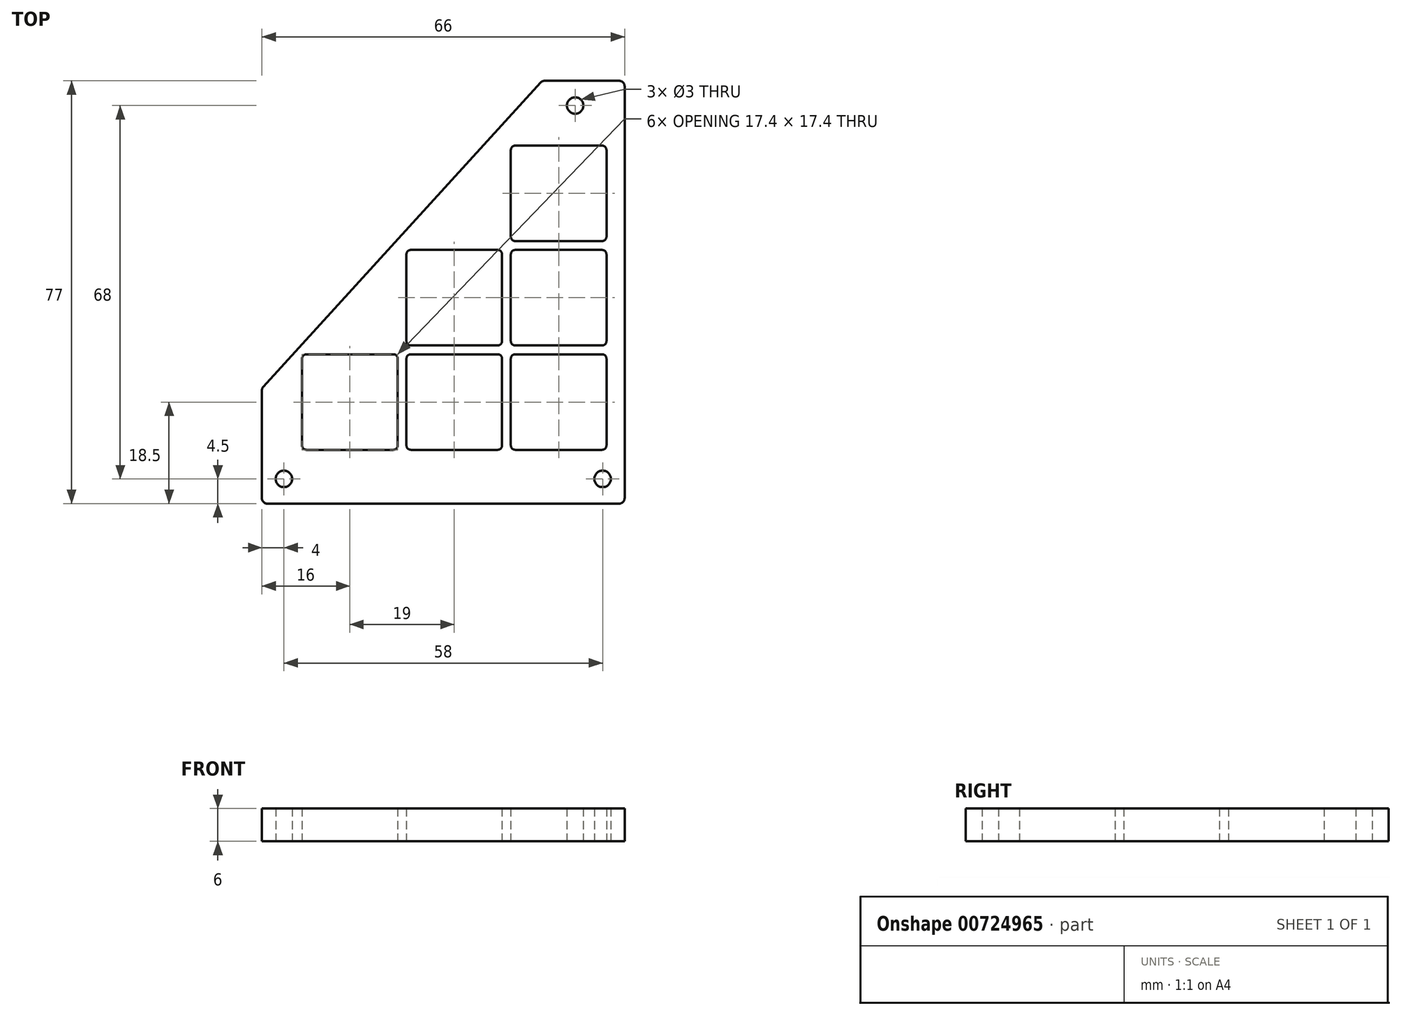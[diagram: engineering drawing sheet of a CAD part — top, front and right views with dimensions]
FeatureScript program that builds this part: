
annotation { "Feature Type Name" : "Feature", "Feature Type Description" : "" }
export const myFeature = defineFeature(function(context is Context, id is Id, definition is map)
    precondition{}
    {
        {
            var Q0;
            Q0=qCreatedBy(makeId("Top.planeOp"),FACE);
            var sketch = newSketch(context, id + "F0", { "sketchPlane" : qUnion([Q0])});
            skLineSegment(sketch, "E0", {"start": v(0, 0) * mm, "end": v(66, 0) * mm});
            skLineSegment(sketch, "E1", {"start": v(66, 0) * mm, "end": v(66, 77) * mm});
            skLineSegment(sketch, "E2", {"start": v(66, 77) * mm, "end": v(51, 77) * mm});
            skLineSegment(sketch, "E3", {"start": v(0, 0) * mm, "end": v(0, 21) * mm});
            skLineSegment(sketch, "E4", {"start": v(0, 21) * mm, "end": v(51, 77) * mm});
            skCircle(sketch, "E5", {"center": v(4, 4.5) * mm, "radius": 1.5 * mm});
            skCircle(sketch, "E6", {"center": v(57, 72.5) * mm, "radius": 1.5 * mm});
            skCircle(sketch, "E7", {"center": v(62, 4.5) * mm, "radius": 1.5 * mm});
            skLineSegment(sketch, "E8.bottom", {"start": v(24.7, 9.8) * mm, "end": v(7.3, 9.8) * mm});
            skLineSegment(sketch, "E8.top", {"start": v(24.7, 27.2) * mm, "end": v(7.3, 27.2) * mm});
            skLineSegment(sketch, "E8.left", {"start": v(24.7, 9.8) * mm, "end": v(24.7, 27.2) * mm});
            skLineSegment(sketch, "E8.right", {"start": v(7.3, 9.8) * mm, "end": v(7.3, 27.2) * mm});
            skPoint(sketch, "E8.middle", {"position": v(16, 18.5) * mm});
            skLineSegment(sketch, "E9.bottom", {"start": v(43.7, 9.8) * mm, "end": v(26.3, 9.8) * mm});
            skLineSegment(sketch, "E9.top", {"start": v(43.7, 27.2) * mm, "end": v(26.3, 27.2) * mm});
            skLineSegment(sketch, "E9.left", {"start": v(43.7, 9.8) * mm, "end": v(43.7, 27.2) * mm});
            skLineSegment(sketch, "E9.right", {"start": v(26.3, 9.8) * mm, "end": v(26.3, 27.2) * mm});
            skPoint(sketch, "E9.middle", {"position": v(35, 18.5) * mm});
            skLineSegment(sketch, "E10.bottom", {"start": v(62.7, 9.8) * mm, "end": v(45.3, 9.8) * mm});
            skLineSegment(sketch, "E10.top", {"start": v(62.7, 27.2) * mm, "end": v(45.3, 27.2) * mm});
            skLineSegment(sketch, "E10.left", {"start": v(62.7, 9.8) * mm, "end": v(62.7, 27.2) * mm});
            skLineSegment(sketch, "E10.right", {"start": v(45.3, 9.8) * mm, "end": v(45.3, 27.2) * mm});
            skPoint(sketch, "E10.middle", {"position": v(54, 18.5) * mm});
            skLineSegment(sketch, "E11.bottom", {"start": v(43.7, 28.8) * mm, "end": v(26.3, 28.8) * mm});
            skLineSegment(sketch, "E11.top", {"start": v(43.7, 46.2) * mm, "end": v(26.3, 46.2) * mm});
            skLineSegment(sketch, "E11.left", {"start": v(43.7, 28.8) * mm, "end": v(43.7, 46.2) * mm});
            skLineSegment(sketch, "E11.right", {"start": v(26.3, 28.8) * mm, "end": v(26.3, 46.2) * mm});
            skPoint(sketch, "E11.middle", {"position": v(35, 37.5) * mm});
            skLineSegment(sketch, "E12.bottom", {"start": v(62.7, 28.8) * mm, "end": v(45.3, 28.8) * mm});
            skLineSegment(sketch, "E12.top", {"start": v(62.7, 46.2) * mm, "end": v(45.3, 46.2) * mm});
            skLineSegment(sketch, "E12.left", {"start": v(62.7, 28.8) * mm, "end": v(62.7, 46.2) * mm});
            skLineSegment(sketch, "E12.right", {"start": v(45.3, 28.8) * mm, "end": v(45.3, 46.2) * mm});
            skPoint(sketch, "E12.middle", {"position": v(54, 37.5) * mm});
            skLineSegment(sketch, "E13.bottom", {"start": v(62.7, 47.8) * mm, "end": v(45.3, 47.8) * mm});
            skLineSegment(sketch, "E13.top", {"start": v(62.7, 65.2) * mm, "end": v(45.3, 65.2) * mm});
            skLineSegment(sketch, "E13.left", {"start": v(62.7, 47.8) * mm, "end": v(62.7, 65.2) * mm});
            skLineSegment(sketch, "E13.right", {"start": v(45.3, 47.8) * mm, "end": v(45.3, 65.2) * mm});
            skPoint(sketch, "E13.middle", {"position": v(54, 56.5) * mm});
            skSolve(sketch);
        }
        {
            var Q0;
            Q0=makeQuery(id+"F0.imprint","IMPRINT",FACE,{"disambiguationData":[TD([[makeQuery(id+"F0.imprint","IMPRINT",EDGE,{"derivedFrom":sQuery(id+"F0.wireOp",EDGE,"E0")}),1.0]])]});
            extrude(context, id + "F1", {"entities" : qUnion([Q0]), "depth" : 6 * mm, "offsetDistance" : 25 * mm});
        }
        {
            var Q0;
            Q0=makeQuery(id+"F1.opExtrude","SWEPT_EDGE",EDGE,{"disambiguationData":[OSD([sQuery(id+"F0.wireOp",EDGE,"E8.top"),sQuery(id+"F0.wireOp",EDGE,"E8.right")])]});
            var Q1;
            Q1=makeQuery(id+"F1.opExtrude","SWEPT_EDGE",EDGE,{"disambiguationData":[OSD([sQuery(id+"F0.wireOp",EDGE,"E9.top"),sQuery(id+"F0.wireOp",EDGE,"E9.right")])]});
            var Q2;
            Q2=makeQuery(id+"F1.opExtrude","SWEPT_EDGE",EDGE,{"disambiguationData":[OSD([sQuery(id+"F0.wireOp",EDGE,"E10.top"),sQuery(id+"F0.wireOp",EDGE,"E10.right")])]});
            var Q3;
            Q3=makeQuery(id+"F1.opExtrude","SWEPT_EDGE",EDGE,{"disambiguationData":[OSD([sQuery(id+"F0.wireOp",EDGE,"E11.top"),sQuery(id+"F0.wireOp",EDGE,"E11.right")])]});
            var Q4;
            Q4=makeQuery(id+"F1.opExtrude","SWEPT_EDGE",EDGE,{"disambiguationData":[OSD([sQuery(id+"F0.wireOp",EDGE,"E12.top"),sQuery(id+"F0.wireOp",EDGE,"E12.right")])]});
            var Q5;
            Q5=makeQuery(id+"F1.opExtrude","SWEPT_EDGE",EDGE,{"disambiguationData":[OSD([sQuery(id+"F0.wireOp",EDGE,"E13.top"),sQuery(id+"F0.wireOp",EDGE,"E13.right")])]});
            var Q6;
            Q6=makeQuery(id+"F1.opExtrude","SWEPT_EDGE",EDGE,{"disambiguationData":[OSD([sQuery(id+"F0.wireOp",EDGE,"E13.top"),sQuery(id+"F0.wireOp",EDGE,"E13.left")])]});
            var Q7;
            Q7=makeQuery(id+"F1.opExtrude","SWEPT_EDGE",EDGE,{"disambiguationData":[OSD([sQuery(id+"F0.wireOp",EDGE,"E12.top"),sQuery(id+"F0.wireOp",EDGE,"E12.left")])]});
            var Q8;
            Q8=makeQuery(id+"F1.opExtrude","SWEPT_EDGE",EDGE,{"disambiguationData":[OSD([sQuery(id+"F0.wireOp",EDGE,"E10.top"),sQuery(id+"F0.wireOp",EDGE,"E10.left")])]});
            var Q9;
            Q9=makeQuery(id+"F1.opExtrude","SWEPT_EDGE",EDGE,{"disambiguationData":[OSD([sQuery(id+"F0.wireOp",EDGE,"E11.top"),sQuery(id+"F0.wireOp",EDGE,"E11.left")])]});
            var Q10;
            Q10=makeQuery(id+"F1.opExtrude","SWEPT_EDGE",EDGE,{"disambiguationData":[OSD([sQuery(id+"F0.wireOp",EDGE,"E9.top"),sQuery(id+"F0.wireOp",EDGE,"E9.left")])]});
            var Q11;
            Q11=makeQuery(id+"F1.opExtrude","SWEPT_EDGE",EDGE,{"disambiguationData":[OSD([sQuery(id+"F0.wireOp",EDGE,"E8.top"),sQuery(id+"F0.wireOp",EDGE,"E8.left")])]});
            var Q12;
            Q12=makeQuery(id+"F1.opExtrude","SWEPT_EDGE",EDGE,{"disambiguationData":[OSD([sQuery(id+"F0.wireOp",EDGE,"E13.bottom"),sQuery(id+"F0.wireOp",EDGE,"E13.left")])]});
            var Q13;
            Q13=makeQuery(id+"F1.opExtrude","SWEPT_EDGE",EDGE,{"disambiguationData":[OSD([sQuery(id+"F0.wireOp",EDGE,"E12.bottom"),sQuery(id+"F0.wireOp",EDGE,"E12.left")])]});
            var Q14;
            Q14=makeQuery(id+"F1.opExtrude","SWEPT_EDGE",EDGE,{"disambiguationData":[OSD([sQuery(id+"F0.wireOp",EDGE,"E10.bottom"),sQuery(id+"F0.wireOp",EDGE,"E10.left")])]});
            var Q15;
            Q15=makeQuery(id+"F1.opExtrude","SWEPT_EDGE",EDGE,{"disambiguationData":[OSD([sQuery(id+"F0.wireOp",EDGE,"E9.bottom"),sQuery(id+"F0.wireOp",EDGE,"E9.left")])]});
            var Q16;
            Q16=makeQuery(id+"F1.opExtrude","SWEPT_EDGE",EDGE,{"disambiguationData":[OSD([sQuery(id+"F0.wireOp",EDGE,"E8.bottom"),sQuery(id+"F0.wireOp",EDGE,"E8.left")])]});
            var Q17;
            Q17=makeQuery(id+"F1.opExtrude","SWEPT_EDGE",EDGE,{"disambiguationData":[OSD([sQuery(id+"F0.wireOp",EDGE,"E11.bottom"),sQuery(id+"F0.wireOp",EDGE,"E11.left")])]});
            var Q18;
            Q18=makeQuery(id+"F1.opExtrude","SWEPT_EDGE",EDGE,{"disambiguationData":[OSD([sQuery(id+"F0.wireOp",EDGE,"E11.bottom"),sQuery(id+"F0.wireOp",EDGE,"E11.right")])]});
            var Q19;
            Q19=makeQuery(id+"F1.opExtrude","SWEPT_EDGE",EDGE,{"disambiguationData":[OSD([sQuery(id+"F0.wireOp",EDGE,"E9.bottom"),sQuery(id+"F0.wireOp",EDGE,"E9.right")])]});
            var Q20;
            Q20=makeQuery(id+"F1.opExtrude","SWEPT_EDGE",EDGE,{"disambiguationData":[OSD([sQuery(id+"F0.wireOp",EDGE,"E8.bottom"),sQuery(id+"F0.wireOp",EDGE,"E8.right")])]});
            var Q21;
            Q21=makeQuery(id+"F1.opExtrude","SWEPT_EDGE",EDGE,{"disambiguationData":[OSD([sQuery(id+"F0.wireOp",EDGE,"E10.bottom"),sQuery(id+"F0.wireOp",EDGE,"E10.right")])]});
            var Q22;
            Q22=makeQuery(id+"F1.opExtrude","SWEPT_EDGE",EDGE,{"disambiguationData":[OSD([sQuery(id+"F0.wireOp",EDGE,"E12.bottom"),sQuery(id+"F0.wireOp",EDGE,"E12.right")])]});
            var Q23;
            Q23=makeQuery(id+"F1.opExtrude","SWEPT_EDGE",EDGE,{"disambiguationData":[OSD([sQuery(id+"F0.wireOp",EDGE,"E13.bottom"),sQuery(id+"F0.wireOp",EDGE,"E13.right")])]});
            fillet(context, id + "F2", {"entities" : qUnion([Q0, Q1, Q2, Q3, Q4, Q5, Q6, Q7, Q8, Q9, Q10, Q11, Q12, Q13, Q14, Q15, Q16, Q17, Q18, Q19, Q20, Q21, Q22, Q23]), "radius" : 0.8 * mm, "tangentPropagation" : true, "allowEdgeOverflow" : false});
        }
        {
            var Q0;
            Q0=makeQuery(id+"F1.opExtrude","SWEPT_EDGE",EDGE,{"disambiguationData":[OSD([sQuery(id+"F0.wireOp",EDGE,"E1"),sQuery(id+"F0.wireOp",EDGE,"E2")])]});
            var Q1;
            Q1=makeQuery(id+"F1.opExtrude","SWEPT_EDGE",EDGE,{"disambiguationData":[OSD([sQuery(id+"F0.wireOp",EDGE,"E2"),sQuery(id+"F0.wireOp",EDGE,"E4")])]});
            var Q2;
            Q2=makeQuery(id+"F1.opExtrude","SWEPT_EDGE",EDGE,{"disambiguationData":[OSD([sQuery(id+"F0.wireOp",EDGE,"E3"),sQuery(id+"F0.wireOp",EDGE,"E4")])]});
            var Q3;
            Q3=makeQuery(id+"F1.opExtrude","SWEPT_EDGE",EDGE,{"disambiguationData":[OSD([sQuery(id+"F0.wireOp",EDGE,"E0"),sQuery(id+"F0.wireOp",EDGE,"E3")])]});
            var Q4;
            Q4=makeQuery(id+"F1.opExtrude","SWEPT_EDGE",EDGE,{"disambiguationData":[OSD([sQuery(id+"F0.wireOp",EDGE,"E0"),sQuery(id+"F0.wireOp",EDGE,"E1")])]});
            fillet(context, id + "F3", {"entities" : qUnion([Q0, Q1, Q2, Q3, Q4]), "radius" : 1 * mm, "tangentPropagation" : true, "allowEdgeOverflow" : false});
        }
    });
